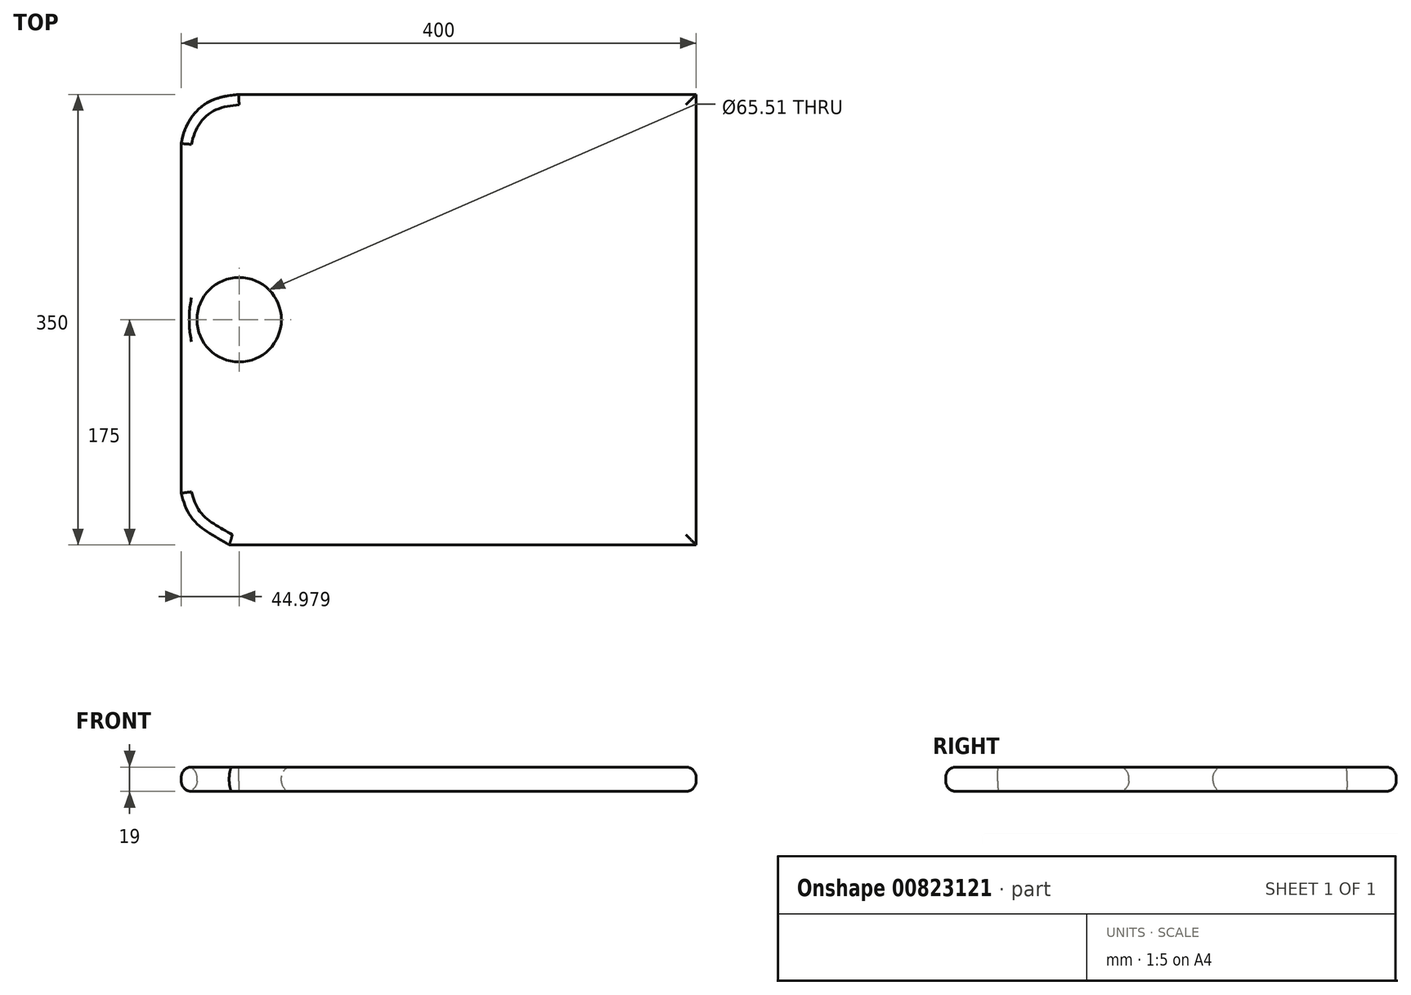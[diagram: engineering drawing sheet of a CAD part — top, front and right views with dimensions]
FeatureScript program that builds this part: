
annotation { "Feature Type Name" : "Feature", "Feature Type Description" : "" }
export const myFeature = defineFeature(function(context is Context, id is Id, definition is map)
    precondition{}
    {
        {
            var Q0;
            Q0=qCreatedBy(makeId("Top.planeOp"),FACE);
            var sketch = newSketch(context, id + "F0", { "sketchPlane" : qUnion([Q0])});
            skLineSegment(sketch, "E0.bottom", {"start": v(200, 175) * mm, "end": v(-200, 175) * mm});
            skLineSegment(sketch, "E0.top", {"start": v(200, -175) * mm, "end": v(-200, -175) * mm});
            skLineSegment(sketch, "E0.left", {"start": v(200, 175) * mm, "end": v(200, -175) * mm});
            skLineSegment(sketch, "E0.right", {"start": v(-200, 175) * mm, "end": v(-200, -175) * mm});
            skPoint(sketch, "E0.middle", {"position": v(0, 0) * mm});
            skSolve(sketch);
        }
        {
            var Q0;
            Q0 = qSketchRegion(id + "F0", true);
            extrude(context, id + "F1", {"entities" : qUnion([Q0]), "depth" : 19 * mm, "offsetDistance" : 25 * mm});
        }
        {
            var Q0;
            Q0=makeQuery(id+"F1.opExtrude","CAP_FACE",FACE,{"disambiguationData":[OSD([sQuery(id+"F0.wireOp",EDGE,"E0.bottom"),sQuery(id+"F0.wireOp",EDGE,"E0.top"),sQuery(id+"F0.wireOp",EDGE,"E0.left"),sQuery(id+"F0.wireOp",EDGE,"E0.right")])],"isStart":false});
            var sketch = newSketch(context, id + "F2", { "sketchPlane" : qUnion([Q0])});
            skFitSpline(sketch, "E1", {"points": [v(-155.44, 175) * mm, v(-184.8, 165.14) * mm, v(-200, 136.83) * mm], "startDerivative": vector(-78.43, -7) * mm, "endDerivative": vector(-9.77, -70.2) * mm});
            skFitSpline(sketch, "E2", {"points": [v(-200, -134.73) * mm, v(-186.9, -159.37) * mm, v(-162.78, -175) * mm, v(-163.83, -175) * mm], "startDerivative": vector(14.9, -56.12) * mm, "endDerivative": vector(-18.26, 2.59) * mm});
            skCircle(sketch, "E3", {"center": v(-155.02, 0) * mm, "radius": 32.76 * mm});
            skSolve(sketch);
        }
        {
            var Q0;
            Q0=makeQuery(id+"F2.imprint","IMPRINT",FACE,{"disambiguationData":[TD([[makeQuery(id+"F2.imprint","IMPRINT",EDGE,{"derivedFrom":sQuery(id+"F2.wireOp",EDGE,"E3")}),1.0]])]});
            var Q1;
            {var subQ0=sQuery(id+"F2.wireOp",EDGE,"E2");var subQ1=makeQuery(id+"F1.opExtrude","CAP_EDGE",EDGE,{"disambiguationData":[OSD([sQuery(id+"F0.wireOp",EDGE,"E0.right")])],"isStart":false});var subQ2=makeQuery(id+"F2.imprint","INTERSECT",VERTEX,{"derivedFrom":[subQ1,subQ0]});Q1=makeQuery(id+"F2.imprint","IMPRINT",FACE,{"disambiguationData":[TD([[makeQuery(id+"F2.imprint","IMPRINT",EDGE,{"disambiguationData":[TD([[subQ2,-1.0]])],"derivedFrom":subQ0}),-1.0]])]});}
            var Q2;
            {var subQ0=sQuery(id+"F2.wireOp",EDGE,"E1");Q2=makeQuery(id+"F2.imprint","IMPRINT",FACE,{"disambiguationData":[TD([[makeQuery(id+"F2.imprint","IMPRINT",EDGE,{"derivedFrom":subQ0}),-1.0]])]});}
            extrude(context, id + "F3", {"entities" : qUnion([Q0, Q1, Q2]), "operationType" : NewBodyOperationType.REMOVE, "oppositeDirection" : true, "depth" : 25 * mm, "offsetDistance" : 25 * mm});
        }
        {
            var Q0;
            Q0=makeQuery(id+"F1.opExtrude","CAP_FACE",FACE,{"disambiguationData":[OSD([sQuery(id+"F0.wireOp",EDGE,"E0.bottom"),sQuery(id+"F0.wireOp",EDGE,"E0.top"),sQuery(id+"F0.wireOp",EDGE,"E0.left"),sQuery(id+"F0.wireOp",EDGE,"E0.right")])],"isStart":false});
            fillet(context, id + "F4", {"entities" : qUnion([Q0]), "radius" : 8 * mm, "tangentPropagation" : true, "allowEdgeOverflow" : false});
        }
        {
            var Q0;
            Q0=makeQuery(id+"F1.opExtrude","CAP_FACE",FACE,{"disambiguationData":[OSD([sQuery(id+"F0.wireOp",EDGE,"E0.bottom"),sQuery(id+"F0.wireOp",EDGE,"E0.top"),sQuery(id+"F0.wireOp",EDGE,"E0.left"),sQuery(id+"F0.wireOp",EDGE,"E0.right")])],"isStart":true});
            fillet(context, id + "F5", {"entities" : qUnion([Q0]), "radius" : 8 * mm, "tangentPropagation" : true, "allowEdgeOverflow" : false});
        }
    });
